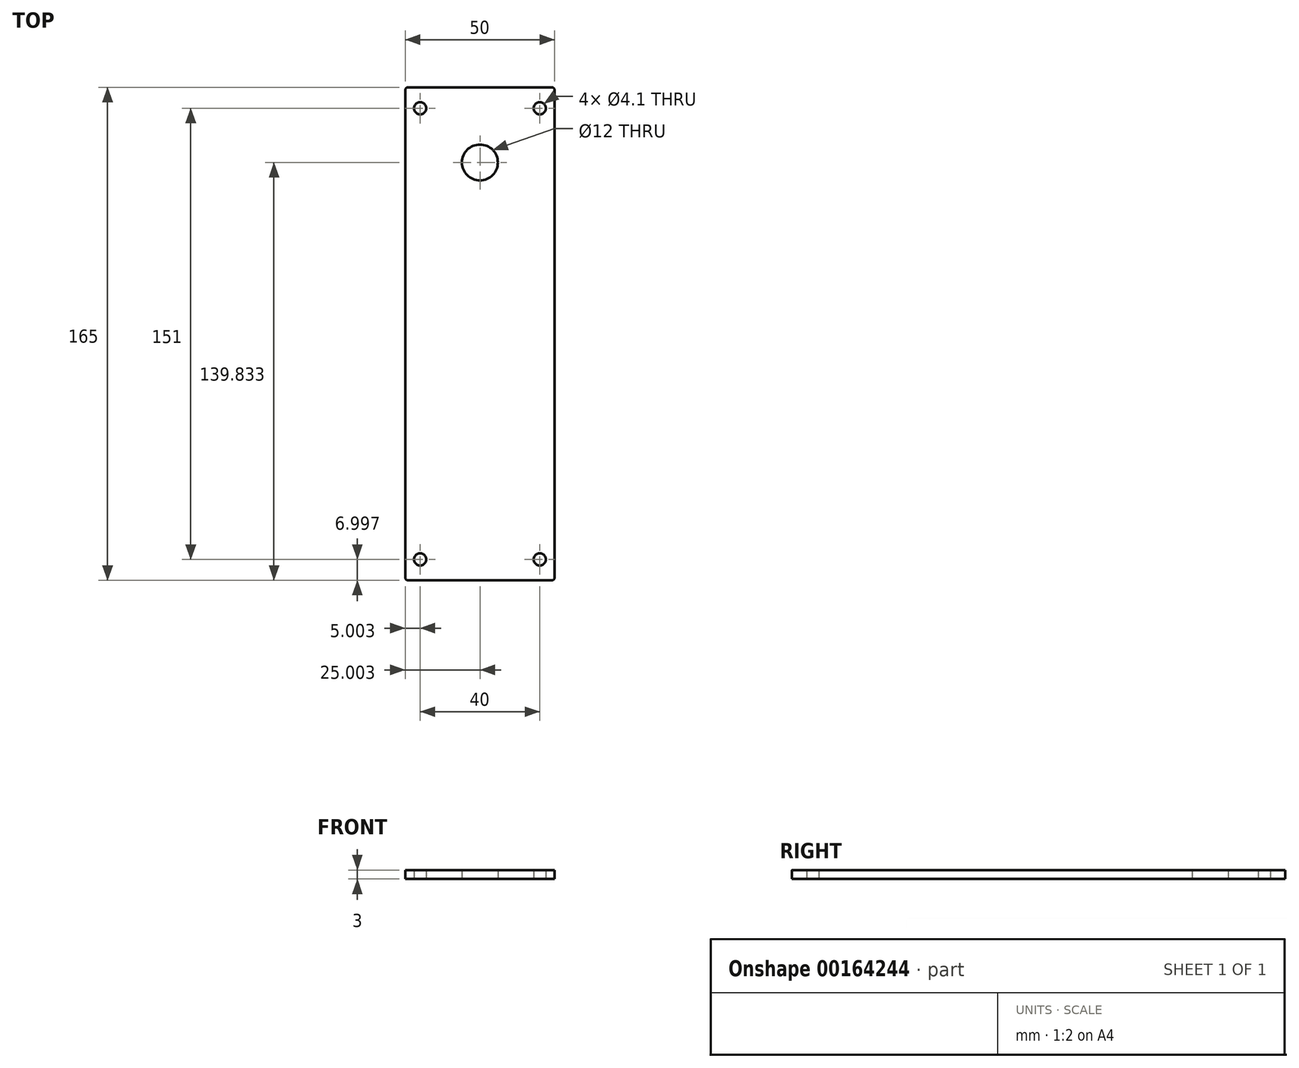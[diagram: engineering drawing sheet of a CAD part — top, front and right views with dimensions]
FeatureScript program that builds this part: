
annotation { "Feature Type Name" : "Feature", "Feature Type Description" : "" }
export const myFeature = defineFeature(function(context is Context, id is Id, definition is map)
    precondition{}
    {
        {
            var Q0;
            Q0=qCreatedBy(makeId("Top.planeOp"),FACE);
            var sketch = newSketch(context, id + "F0", { "sketchPlane" : qUnion([Q0])});
            skLineSegment(sketch, "E0.bottom", {"start": v(-59.86, 99.3) * mm, "end": v(-11.86, 99.3) * mm});
            skLineSegment(sketch, "E0.top", {"start": v(-59.86, -65.7) * mm, "end": v(-11.86, -65.7) * mm});
            skLineSegment(sketch, "E0.left", {"start": v(-60.86, 98.3) * mm, "end": v(-60.86, -64.7) * mm});
            skLineSegment(sketch, "E0.right", {"start": v(-10.86, 98.3) * mm, "end": v(-10.86, -64.7) * mm});
            skPoint(sketch, "E1.visualSharp", {"position": v(-60.86, 99.3) * mm});
            skArc(sketch, "E1.filletArc", {"start": v(-59.86, 99.3) * mm, "mid": v(-60.56, 99.01) * mm, "end": v(-60.86, 98.3) * mm});
            skPoint(sketch, "E2.visualSharp", {"position": v(-10.86, 99.3) * mm});
            skArc(sketch, "E2.filletArc", {"start": v(-10.86, 98.3) * mm, "mid": v(-11.15, 99.01) * mm, "end": v(-11.86, 99.3) * mm});
            skPoint(sketch, "E3.visualSharp", {"position": v(-60.86, -65.7) * mm});
            skArc(sketch, "E3.filletArc", {"start": v(-60.86, -64.7) * mm, "mid": v(-60.56, -65.4) * mm, "end": v(-59.86, -65.7) * mm});
            skPoint(sketch, "E4.visualSharp", {"position": v(-10.86, -65.7) * mm});
            skArc(sketch, "E4.filletArc", {"start": v(-11.86, -65.7) * mm, "mid": v(-11.15, -65.4) * mm, "end": v(-10.86, -64.7) * mm});
            skCircle(sketch, "E5", {"center": v(-55.86, -58.7) * mm, "radius": 2.05 * mm});
            skCircle(sketch, "E6", {"center": v(-15.86, -58.7) * mm, "radius": 2.05 * mm});
            skCircle(sketch, "E7", {"center": v(-55.86, 92.3) * mm, "radius": 2.05 * mm});
            skCircle(sketch, "E8", {"center": v(-15.86, 92.3) * mm, "radius": 2.05 * mm});
            skLineSegment(sketch, "E9", {"start": v(-55.86, -58.7) * mm, "end": v(-55.86, 92.3) * mm, "construction": true});
            skLineSegment(sketch, "E10", {"start": v(-55.86, -58.7) * mm, "end": v(-15.86, -58.7) * mm, "construction": true});
            skLineSegment(sketch, "E11", {"start": v(-55.86, 92.3) * mm, "end": v(-15.86, 92.3) * mm, "construction": true});
            skLineSegment(sketch, "E12", {"start": v(-15.86, 92.3) * mm, "end": v(-15.86, -58.7) * mm, "construction": true});
            skSolve(sketch);
        }
        {
            var Q0;
            Q0=makeQuery(id+"F0.imprint","IMPRINT",FACE,{"disambiguationData":[TD([[makeQuery(id+"F0.imprint","IMPRINT",EDGE,{"derivedFrom":sQuery(id+"F0.wireOp",EDGE,"E0.bottom")}),-1.0]])]});
            extrude(context, id + "F1", {"entities" : qUnion([Q0]), "depth" : 3 * mm});
        }
        {
            var Q0;
            Q0=qCreatedBy(makeId("Top.planeOp"),FACE);
            var sketch = newSketch(context, id + "F2", { "sketchPlane" : qUnion([Q0])});
            skCircle(sketch, "E13", {"center": v(-35.86, 74.14) * mm, "radius": 6 * mm});
            skLineSegment(sketch, "E14.0", {"start": v(-60.86, 98.3) * mm, "end": v(-60.86, -64.7) * mm, "construction": true});
            skLineSegment(sketch, "E14.1", {"start": v(-10.86, 98.3) * mm, "end": v(-10.86, -64.7) * mm, "construction": true});
            skLineSegment(sketch, "E14.2", {"start": v(-59.86, 99.3) * mm, "end": v(-11.86, 99.3) * mm, "construction": true});
            skLineSegment(sketch, "E15", {"start": v(-35.86, 99.3) * mm, "end": v(-35.86, -85.91) * mm, "construction": true});
            skLineSegment(sketch, "E16", {"start": v(-60.86, 16.8) * mm, "end": v(91.4, 16.8) * mm, "construction": true});
            skPoint(sketch, "E17", {"position": v(-35.86, 6.7) * mm});
            skSolve(sketch);
        }
        {
            var Q0;
            Q0 = qSketchRegion(id + "F2", true);
            extrude(context, id + "F3", {"entities" : qUnion([Q0]), "operationType" : NewBodyOperationType.REMOVE, "depth" : 25 * mm});
        }
    });
